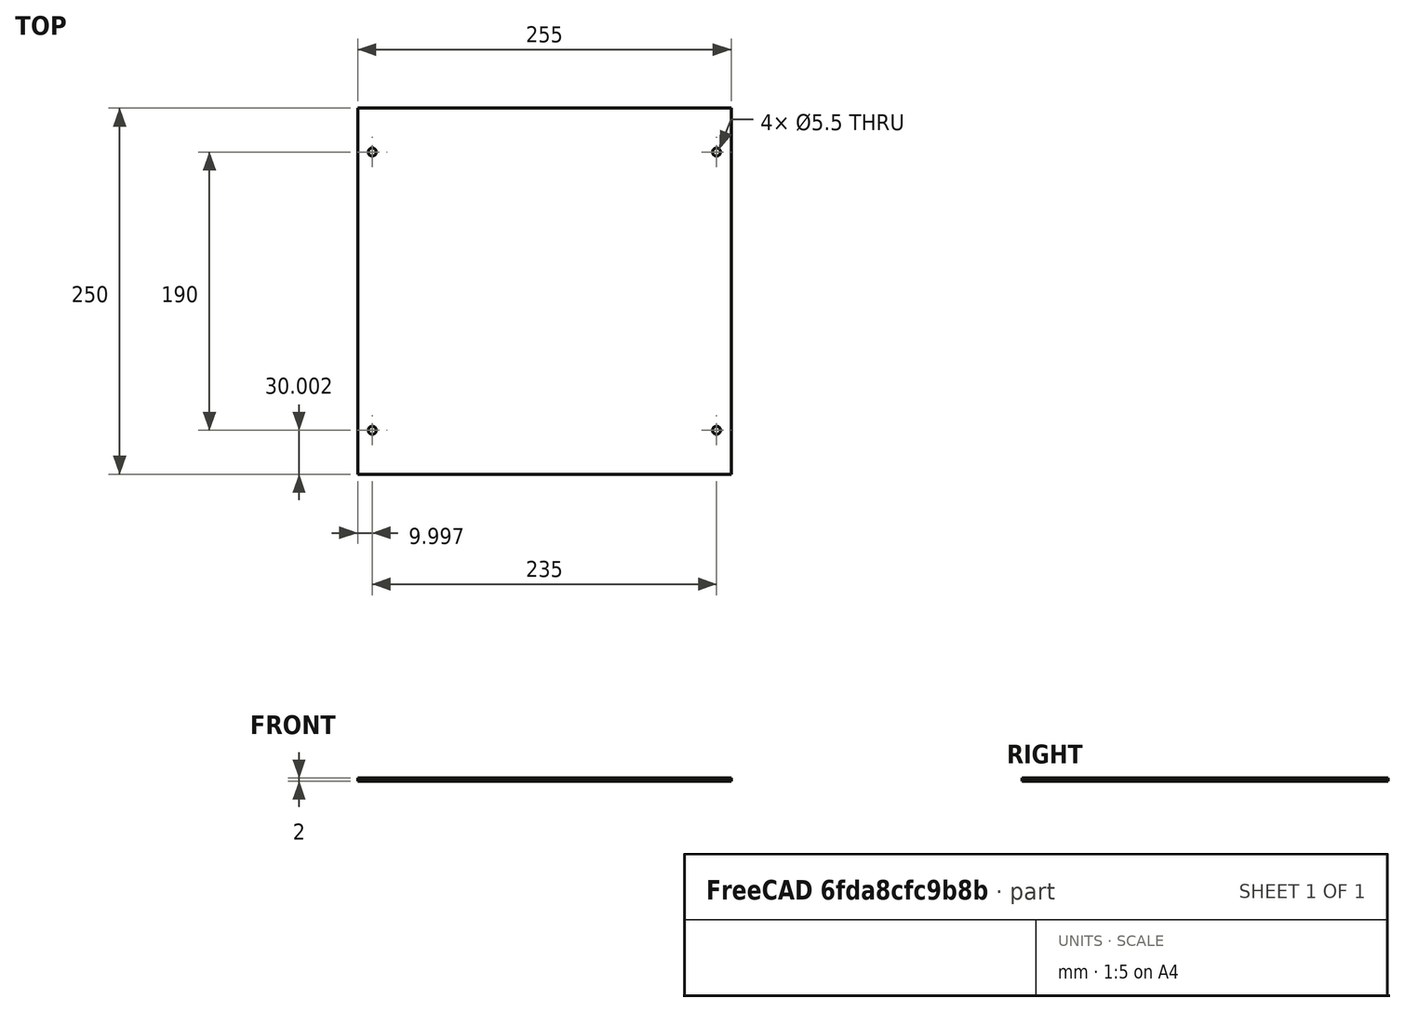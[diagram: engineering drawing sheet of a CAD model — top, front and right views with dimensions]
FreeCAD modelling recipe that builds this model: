
FCSTD DOCUMENT  (FreeCAD 0.15R4671 (Git))
Label: side
License: All rights reserved
LicenseURL: http://en.wikipedia.org/wiki/All_rights_reserved
objects: Drawing::FeatureViewPython×5, Part::Cylinder×4, Part::Cut×4, Part::Box×1, Drawing::FeatureViewPart×1, Drawing::FeaturePage×1
note: 9 computed .brp shape members not serialized (recipe doc carries the construction recipe); baked Part::Feature solids carry a one-line shape summary decoded from their .brp

FEATURE [Part::Box] Box001  label="Cube001"
  Height = 2
  Length = 255
  Placement = pos=(0,0,1.5332e-08) rot=(0,0,1;0rad)
  Width = 250
FEATURE [Part::Cylinder] Cylinder004
  Angle = 360
  Height = 10
  Placement = pos=(10,30,-5) rot=(0,0,1;0rad)
  Radius = 2.75
FEATURE [Part::Cylinder] Cylinder005
  Angle = 360
  Height = 10
  Placement = pos=(10,220,-5) rot=(0,0,1;0rad)
  Radius = 2.75
FEATURE [Part::Cylinder] Cylinder006
  Angle = 360
  Height = 10
  Placement = pos=(245,30,-5) rot=(0,0,1;0rad)
  Radius = 2.75
FEATURE [Part::Cylinder] Cylinder007
  Angle = 360
  Height = 10
  Placement = pos=(245,220,-5) rot=(0,0,1;0rad)
  Radius = 2.75
FEATURE [Part::Cut] Cut004
  Base = -> Box001
  Tool = -> Cylinder004
FEATURE [Part::Cut] Cut005
  Base = -> Cut004
  Tool = -> Cylinder005
FEATURE [Part::Cut] Cut006
  Base = -> Cut005
  Tool = -> Cylinder006
FEATURE [Part::Cut] Cut007  label="side"
  Base = -> Cut006
  Placement = pos=(103.477,-144.038,187.74) rot=(0,0,1;0rad)
  Tool = -> Cylinder007
FEATURE [Drawing::FeatureViewPart] Ortho  label="Ortho_0_0"
  Direction = (0,0,-1)
  HiddenWidth = 0.15
  LineWidth = 0.35
  Rotation = 180
  Scale = 0.5
  ShowHiddenLines = false
  ShowSmoothLines = false
  Source = -> Cut007
  Tolerance = 0.05
  ViewResult = <g id="Ortho_0_0"\n   transform="rotate(180,-5.48833,128.019) translate(-5.48833,128.019) scale(0.5,0.5)"\n  >\n<g   stroke="rgb(0, 0, 0)"\n   stroke-width="0.7"\n   stroke-linecap="butt"\n   stroke-linejoin="miter"\n   fill="none"\n   transform="scale(1,-1)"\n  >\n<path id= "1" d=" M -103.477 -144.038 L -103.477 105.962 " />\n<path id= "2" d=" M -103.477 -144.038 L -358.477 -144.038 " />\n<path id= "3" d=" M -103.477 105.962 L -358.477 105.962 " />\n<path id= "4" d=" M -358.477 -144.038 L -358.477 105.962 " />\n<circle cx ="-348.477" cy ="75.962" r ="2.75" /><circle cx ="-113.477" cy ="75.962" r ="2.75" /><circle cx ="-348.477" cy ="-114.038" r ="2.75" /><circle cx ="-113.477" cy ="-114.038" r ="2.75" /></g>\n</g>
  Visible = true
  X = -5.48833
  Y = 128.019
FEATURE [Drawing::FeatureViewPython] dim001  # drawing view (typed FeaturePython)
  Rotation = 0
  ViewResult = <g> \n  <line x1="46.250170" y1="54.000000" x2="46.250170" y2="38.947094" style="stroke:rgb(0,0,255);stroke-width:0.50" />\n<line x1="173.750170" y1="54.000000" x2="173.750170" y2="38.947094" style="stroke:rgb(0,0,255);stroke-width:0.50" />\n<line x1="46.250170" y1="39.947094" x2="173.750170" y2="39.947094" style="stroke:rgb(0,0,255);stroke-width:0.50" /> \n  <polygon points="173.750170,39.947094 170.750170,38.947094 169.750170,39.947094 170.750170,40.947094" style="fill:rgb(0,0,255);stroke:rgb(0,0,255);stroke-width:0" /><polygon points="46.250170,39.947094 49.250170,40.947094 50.250170,39.947094 49.250170,38.947094" style="fill:rgb(0,0,255);stroke:rgb(0,0,255);stroke-width:0" /> \n  <text x="110.000170" y="37.947094" font-family="inherit" font-size="3.6" fill="rgb(0,0,255)" text-anchor="middle" transform="rotate(0.000000 110.000170,37.947094)" >255</text> </g>
  Visible = true
  X = 0
  Y = 0
  arrowL1 = 3
  arrowL2 = 1
  arrowW = 2
  arrow_scheme = 0
  autoPlaceOffset = 2
  autoPlaceText = true
  click1_x = 107.993
  click1_y = 39.9471
  click2_x = 107.993
  click2_y = 39.9471
  comma_decimal_place = false
  dimension_line_overshoot = 1
  gap_datum_points = 2
  halfDimension_linear = false
  lineColor = rgb(0,0,255)
  strokeWidth = 0.5
  textFormat_linear = %(value)f
  textRenderer_color = rgb(0,0,255)
  textRenderer_family = inherit
  textRenderer_size = 3.6
  unit_custom_scale = 1
  unit_scheme = 0
FEATURE [Drawing::FeatureViewPython] dim002  # drawing view (typed FeaturePython)
  Rotation = 0
  ViewResult = <g> \n  <line x1="44.250170" y1="56.000000" x2="31.160796" y2="56.000000" style="stroke:rgb(0,0,255);stroke-width:0.50" />\n<line x1="44.250170" y1="181.000000" x2="31.160796" y2="181.000000" style="stroke:rgb(0,0,255);stroke-width:0.50" />\n<line x1="32.160796" y1="56.000000" x2="32.160796" y2="181.000000" style="stroke:rgb(0,0,255);stroke-width:0.50" /> \n  <polygon points="32.160796,181.000000 33.160796,178.000000 32.160796,177.000000 31.160796,178.000000" style="fill:rgb(0,0,255);stroke:rgb(0,0,255);stroke-width:0" /><polygon points="32.160796,56.000000 31.160796,59.000000 32.160796,60.000000 33.160796,59.000000" style="fill:rgb(0,0,255);stroke:rgb(0,0,255);stroke-width:0" /> \n  <text x="30.160796" y="118.500000" font-family="inherit" font-size="3.6" fill="rgb(0,0,255)" text-anchor="middle" transform="rotate(-90.000000 30.160796,118.500000)" >250</text> </g>
  Visible = true
  X = 0
  Y = 0
  arrowL1 = 3
  arrowL2 = 1
  arrowW = 2
  arrow_scheme = 0
  autoPlaceOffset = 2
  autoPlaceText = true
  click1_x = 32.1608
  click1_y = 97.8365
  click2_x = 32.1608
  click2_y = 97.8365
  comma_decimal_place = false
  dimension_line_overshoot = 1
  gap_datum_points = 2
  halfDimension_linear = false
  lineColor = rgb(0,0,255)
  strokeWidth = 0.5
  textFormat_linear = %(value)f
  textRenderer_color = rgb(0,0,255)
  textRenderer_family = inherit
  textRenderer_size = 3.6
  unit_custom_scale = 1
  unit_scheme = 0
FEATURE [Drawing::FeatureViewPython] dia001  # drawing view (typed FeaturePython)
  Rotation = 0
  ViewResult = <g>  <circle cx ="51.250170" cy ="71.000000" r="0.250000" stroke="none" fill="rgb(0,0,255)" /> \n<line x1="74.477632" y1="63.983057" x2="49.933921" y2="71.397635" style="stroke:rgb(0,0,255);stroke-width:0.50" />\n<polygon points="52.566419,70.602365 55.727424,70.692071 56.395507,69.445610 55.149046,68.777527" style="fill:rgb(0,0,255);stroke:rgb(0,0,255);stroke-width:0" />\n<polygon points="49.933921,71.397635 46.772916,71.307929 46.104833,72.554390 47.351294,73.222473" style="fill:rgb(0,0,255);stroke:rgb(0,0,255);stroke-width:0" />\n<line x1="74.477632" y1="63.983057" x2="81.586860" y2="63.983057" style="stroke:rgb(0,0,255);stroke-width:0.50" />\n<text x="78.032246" y="61.983057" font-family="inherit" font-size="3.6" fill="rgb(0,0,255)" text-anchor="middle" transform="rotate(0.000000 78.032246,61.983057)" >Ø5.5</text> </g>
  Visible = true
  X = 0
  Y = 0
  arrowL1 = 3
  arrowL2 = 1
  arrowW = 2
  arrow_scheme = 0
  autoPlaceOffset = 2
  autoPlaceText = true
  centerPointDia = 0.5
  click1_x = 74.4776
  click1_y = 63.9831
  click2_x = 81.5869
  click2_y = 63.9831
  click3_x = 81.5869
  click3_y = 63.9831
  comma_decimal_place = false
  lineColor = rgb(0,0,255)
  strokeWidth = 0.5
  textFormat_circular = Ø%(value)3.3f
  textRenderer_color = rgb(0,0,255)
  textRenderer_family = inherit
  textRenderer_size = 3.6
  unit_custom_scale = 1
  unit_scheme = 0
FEATURE [Drawing::FeatureViewPython] dimStack001  # drawing view (typed FeaturePython)
  Rotation = 0
  ViewResult = <g> <line x1="170.750171" y1="166.000000" x2="182.806117" y2="166.000000" style="stroke:rgb(0,0,255);stroke-width:0.50" />\n<line x1="175.750171" y1="181.000000" x2="182.806117" y2="181.000000" style="stroke:rgb(0,0,255);stroke-width:0.50" />\n<line x1="181.806117" y1="166.000000" x2="181.806117" y2="181.000000" style="stroke:rgb(0,0,255);stroke-width:0.50" />\n<polygon points="181.806117,166.000000 180.806117,169.000000 181.806117,170.000000 182.806117,169.000000" style="fill:rgb(0,0,255);stroke:rgb(0,0,255);stroke-width:0" />\n<polygon points="181.806117,181.000000 182.806117,178.000000 181.806117,177.000000 180.806117,178.000000" style="fill:rgb(0,0,255);stroke:rgb(0,0,255);stroke-width:0" />\n<text x="179.806117" y="173.500000" font-family="inherit" font-size="3.6" fill="rgb(0,0,255)" text-anchor="middle" transform="rotate(-90.000000 179.806117,173.500000)" >30</text> </g> 
  Visible = true
  X = 0
  Y = 0
  arrowL1 = 3
  arrowL2 = 1
  arrowW = 2
  arrow_scheme = 0
  autoPlaceOffset = 2
  click1_x = 181.806
  click1_y = 176.82
  comma_decimal_place = false
  dimension_line_overshoot = 1
  gap_datum_points = 2
  lineColor = rgb(0,0,255)
  stack_offset = 7
  stack_offset0 = 0
  strokeWidth = 0.5
  textFormat_linear = %(value)f
  textRenderer_color = rgb(0,0,255)
  textRenderer_family = inherit
  textRenderer_size = 3.6
  unit_custom_scale = 1
  unit_scheme = 0
FEATURE [Drawing::FeatureViewPython] dimStack002  # drawing view (typed FeaturePython)
  Rotation = 0
  ViewResult = <g> <line x1="168.750170" y1="168.000001" x2="168.750170" y2="189.170315" style="stroke:rgb(0,0,255);stroke-width:0.50" />\n<line x1="173.750170" y1="183.000001" x2="173.750170" y2="189.170315" style="stroke:rgb(0,0,255);stroke-width:0.50" />\n<line x1="168.750170" y1="188.170315" x2="173.750170" y2="188.170315" style="stroke:rgb(0,0,255);stroke-width:0.50" />\n<polygon points="168.750170,188.170315 165.750170,187.170315 164.750170,188.170315 165.750170,189.170315" style="fill:rgb(0,0,255);stroke:rgb(0,0,255);stroke-width:0" />\n<polygon points="173.750170,188.170315 176.750170,189.170315 177.750170,188.170315 176.750170,187.170315" style="fill:rgb(0,0,255);stroke:rgb(0,0,255);stroke-width:0" />\n<text x="171.250170" y="186.170315" font-family="inherit" font-size="3.6" fill="rgb(0,0,255)" text-anchor="middle" transform="rotate(0.000000 171.250170,186.170315)" >10</text> </g> 
  Visible = true
  X = 0
  Y = 0
  arrowL1 = 3
  arrowL2 = 1
  arrowW = 2
  arrow_scheme = 0
  autoPlaceOffset = 2
  click1_x = 171.965
  click1_y = 188.17
  comma_decimal_place = false
  dimension_line_overshoot = 1
  gap_datum_points = 2
  lineColor = rgb(0,0,255)
  stack_offset = 7
  stack_offset0 = 0
  strokeWidth = 0.5
  textFormat_linear = %(value)f
  textRenderer_color = rgb(0,0,255)
  textRenderer_family = inherit
  textRenderer_size = 3.6
  unit_custom_scale = 1
  unit_scheme = 0
FEATURE [Drawing::FeaturePage] Page
  EditableTexts = Fichou Dimitri | OCLab side | Aluminium - 2 mm thick | Professur für Lebensmittelwissenschaften | Prof. Dr. Gertrud Morlock | A4 | X / Y | SCALE | PART NUMBER | DRAWING NUMBER | YYYY-MM-DD | A
  Group = -> [Ortho,dim001,dim002,dia001,dimStack001,dimStack002]
  Template = <path>
note: 1 file-system path scrubbed to <path> (originals preserved in the JSON sidecar)
